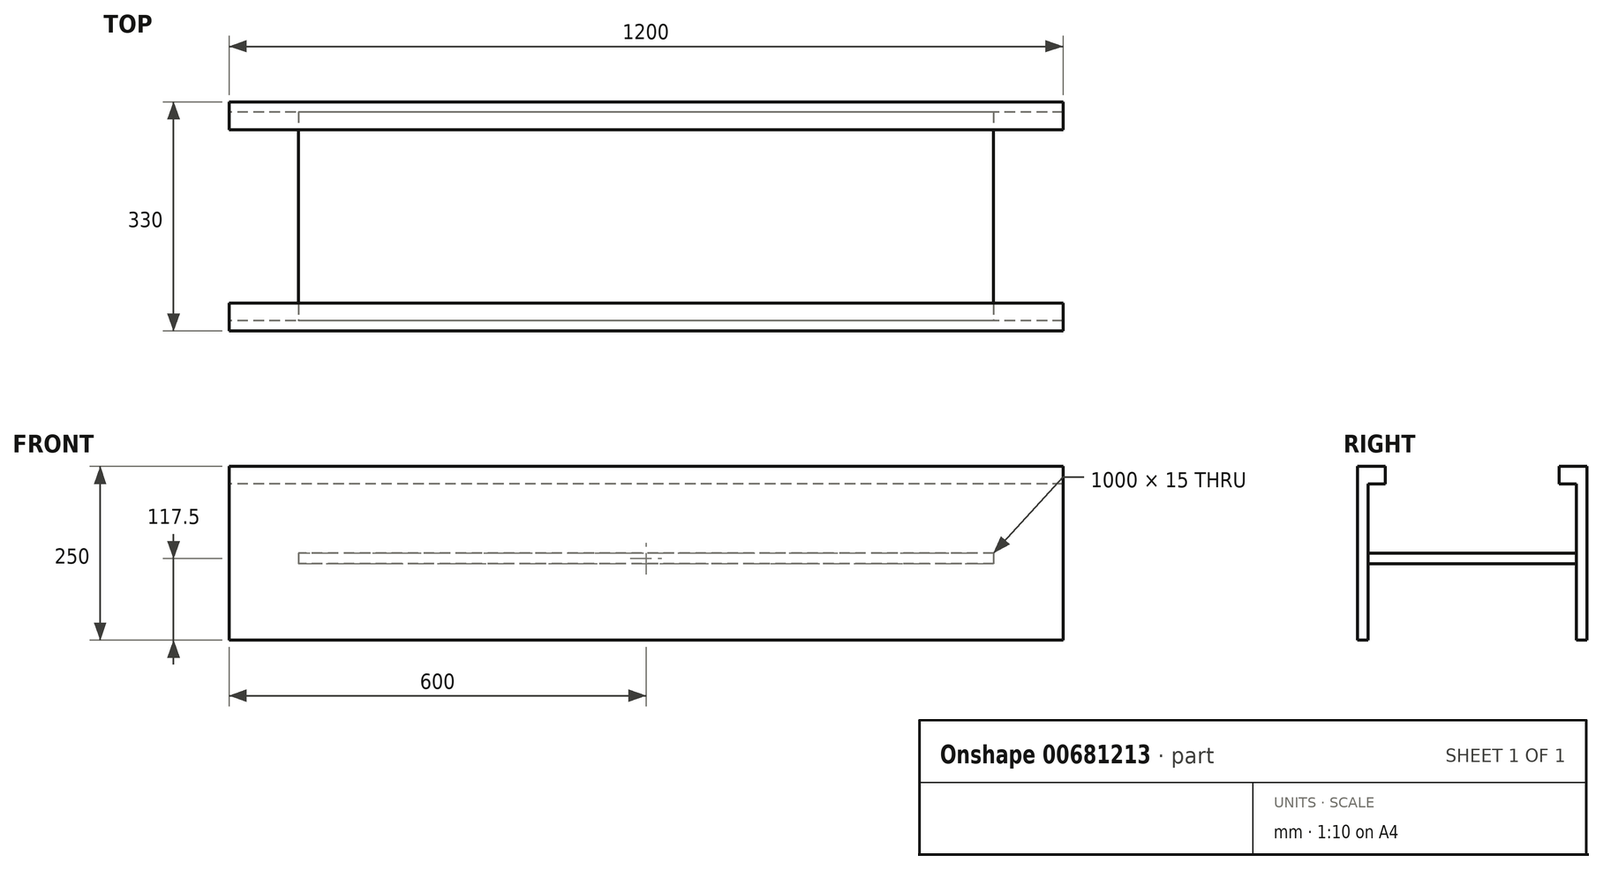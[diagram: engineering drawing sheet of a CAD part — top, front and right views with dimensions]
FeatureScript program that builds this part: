
annotation { "Feature Type Name" : "Feature", "Feature Type Description" : "" }
export const myFeature = defineFeature(function(context is Context, id is Id, definition is map)
    precondition{}
    {
        {
            var Q0;
            Q0=qCreatedBy(makeId("Front.planeOp"),FACE);
            var sketch = newSketch(context, id + "F0", { "sketchPlane" : qUnion([Q0])});
            skLineSegment(sketch, "E0.bottom", {"start": v(-600, -125) * mm, "end": v(600, -125) * mm});
            skLineSegment(sketch, "E0.top", {"start": v(-600, 125) * mm, "end": v(600, 125) * mm});
            skLineSegment(sketch, "E0.left", {"start": v(-600, -125) * mm, "end": v(-600, 125) * mm});
            skLineSegment(sketch, "E0.right", {"start": v(600, -125) * mm, "end": v(600, 125) * mm});
            skSolve(sketch);
        }
        {
            var Q0;
            Q0=makeQuery(id+"F0.imprint","IMPRINT",FACE,{"disambiguationData":[TD([[makeQuery(id+"F0.imprint","IMPRINT",EDGE,{"derivedFrom":sQuery(id+"F0.wireOp",EDGE,"E0.bottom")}),1.0]])]});
            extrude(context, id + "F1", {"entities" : qUnion([Q0]), "oppositeDirection" : true, "depth" : 15 * mm, "offsetDistance" : 25 * mm});
        }
        {
            var Q0;
            Q0=makeQuery(id+"F1.opExtrude","CAP_FACE",FACE,{"disambiguationData":[OSD([sQuery(id+"F0.wireOp",EDGE,"E0.bottom"),sQuery(id+"F0.wireOp",EDGE,"E0.top"),sQuery(id+"F0.wireOp",EDGE,"E0.left"),sQuery(id+"F0.wireOp",EDGE,"E0.right")])],"isStart":false});
            var sketch = newSketch(context, id + "F2", { "sketchPlane" : qUnion([Q0])});
            skLineSegment(sketch, "E1.bottom", {"start": v(-600, 100) * mm, "end": v(600, 100) * mm});
            skLineSegment(sketch, "E1.top", {"start": v(-600, 125) * mm, "end": v(600, 125) * mm});
            skLineSegment(sketch, "E1.left", {"start": v(-600, 100) * mm, "end": v(-600, 125) * mm});
            skLineSegment(sketch, "E1.right", {"start": v(600, 100) * mm, "end": v(600, 125) * mm});
            skSolve(sketch);
        }
        {
            var Q0;
            Q0=makeQuery(id+"F2.imprint","IMPRINT",FACE,{"disambiguationData":[TD([[makeQuery(id+"F2.imprint","IMPRINT",EDGE,{"derivedFrom":sQuery(id+"F2.wireOp",EDGE,"E1.bottom")}),1.0]])]});
            extrude(context, id + "F3", {"entities" : qUnion([Q0]), "operationType" : NewBodyOperationType.ADD, "depth" : 25 * mm, "offsetDistance" : 25 * mm});
        }
        {
            var Q0;
            Q0=makeQuery(id+"F1.opExtrude","CAP_FACE",FACE,{"disambiguationData":[OSD([sQuery(id+"F0.wireOp",EDGE,"E0.bottom"),sQuery(id+"F0.wireOp",EDGE,"E0.top"),sQuery(id+"F0.wireOp",EDGE,"E0.left"),sQuery(id+"F0.wireOp",EDGE,"E0.right")])],"isStart":false});
            var sketch = newSketch(context, id + "F4", { "sketchPlane" : qUnion([Q0])});
            skLineSegment(sketch, "E2.bottom", {"start": v(-500, 0) * mm, "end": v(500, 0) * mm});
            skLineSegment(sketch, "E2.top", {"start": v(-500, -15) * mm, "end": v(500, -15) * mm});
            skLineSegment(sketch, "E2.left", {"start": v(-500, 0) * mm, "end": v(-500, -15) * mm});
            skLineSegment(sketch, "E2.right", {"start": v(500, 0) * mm, "end": v(500, -15) * mm});
            skSolve(sketch);
        }
        {
            var Q0;
            Q0=makeQuery(id+"F4.imprint","IMPRINT",FACE,{"disambiguationData":[TD([[makeQuery(id+"F4.imprint","IMPRINT",EDGE,{"derivedFrom":sQuery(id+"F4.wireOp",EDGE,"E2.bottom")}),-1.0]])]});
            extrude(context, id + "F5", {"entities" : qUnion([Q0]), "operationType" : NewBodyOperationType.ADD, "depth" : 150 * mm, "offsetDistance" : 25 * mm});
        }
        {
            var Q0;
            Q0=makeQuery(id+"F1.opExtrude","SWEPT_BODY",BODY,{"disambiguationData":[OSD([sQuery(id+"F0.wireOp",EDGE,"E0.bottom"),sQuery(id+"F0.wireOp",EDGE,"E0.top"),sQuery(id+"F0.wireOp",EDGE,"E0.left"),sQuery(id+"F0.wireOp",EDGE,"E0.right")])]});
            var Q1;
            Q1=makeQuery(id+"F5.opExtrude","CAP_FACE",FACE,{"disambiguationData":[OSD([sQuery(id+"F4.wireOp",EDGE,"E2.bottom"),sQuery(id+"F4.wireOp",EDGE,"E2.top"),sQuery(id+"F4.wireOp",EDGE,"E2.left"),sQuery(id+"F4.wireOp",EDGE,"E2.right")])],"isStart":false});
            mirror(context, id + "F6", {"operationType" : NewBodyOperationType.ADD, "entities" : qUnion([Q0]), "mirrorPlane" : qUnion([Q1])});
        }
    });
